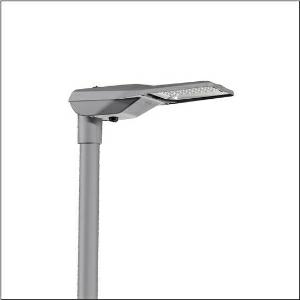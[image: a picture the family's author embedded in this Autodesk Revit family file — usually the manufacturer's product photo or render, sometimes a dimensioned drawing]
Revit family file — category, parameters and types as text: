
# Revit family: streetlight_sl_21_mini___stw1_0a_5xe2e63t08hb_eb5d
name_source: partatom
category: Lighting Fixtures
units: mm (PartAtom-declared; Revit-internal decimal feet)

## family parameters
Cut with Voids When Loaded = No
Host = Face
Light Source = No
Part Type = Normal
Room Calculation Point = No
Round Connector Dimension = Use Diameter
Shared = No

## types (1)
- --- (1 x LED, 8110 lm, 66 W, 2700K)
    Apparent Load = 66 VA
    CIE Flux Codes = 38 75 98 100 100
    Color Rendering = 70
    Color Temperature = 2700K
    Default Elevation = 1800 mm
    Description = Streetlight SL 21 mini, mast luminaire, primary light control with lens, of PMMA, primary optical cover: cover, of toughened safety glass, transparent, light distribution: STW1.0a, light emission: direct distribution, primary light characteristic: asymmetric, installation type: side-entry, post-top, LED, High Power LED, rated luminous flux: 8.110lm, luminous efficacy: 123lm/W, light colour: 727, colour temperature: 2700K, control gear: D4i, control: overheat protection, constant luminous flux control, time-dependent luminous flux control, flexible luminous flux parameterisation, pre-setting: logarithmic dimming characteristic, mains connection: 220..240V, AC, 50/60Hz, start of lifetime: 66W, end of service life: 69W, reduction: 30W, luminaire housing, of diecast aluminium, powder-coated, Siteco® metallic grey (DB 702S), corrosivity category C5 mid according to DIN EN ISO 12944, please order mast flange separately, inclination adjustable: 0°, 5°, 10°, 15°, sealing non-destructively replaceable, multi-level sealing system, length: 628mm, width: 235mm, height: 110mm, mast flange for spigot size: 42mm (side-entry): 5XC10008XM4, 60/48mm (side-entry/post-top): 5XC10108XM2, 76/60mm (side-entry/post-top): 5XC10108XM1, mounting height: 4..8m, Smart Interface below and above, protection rating (complete): IP66, insulation class (complete): insulation class II (safety insulation), certification: CE, ENEC, ENEC+, VDE, impact resistance: IK10, permissible operating ambient temperature for outdoor applications: -40..+50°C, standard-compliant lighting for roads and squares, packaging unit: 1 piece

Light Distribution: STW1.0a
    Height = 110 mm
    Lamp = 1 x LED
    Lamp Light Flux = 8110 lm
    Lamp Power = 66 W
    Lamp count = 1
    Length = 625 mm
    Luminous efficacy = 123 lm/W
    Manufacturer = Siteco
    ModVariant = No
    Model = 5XE2E63T08HB
    Number of Poles = 1
    OnlyDefault = Yes
    Power Factor = 1
    Product Name = Streetlight SL 21 mini | STW1.0a
    Product group = mast luminaire | pylon top
    ProductGroupID = 6100
    Protection Class = Protection class II
    Protection Degree = IP 66
    RLX_Detail_Level = 1
    RLX_Emergency_Light_Flux = 0 lm
    RLX_Emergency_Type = 0
    RLX_Emergency_Type_DB = No
    RlxData = <blob elided: 26241 chars, md5=2399ad0b>
    Socket = socket
    Standby Power = 0 W
    System Light Flux = 8110 lm
    System Power = 66 W
    Type Comments = factory setting: luminous flux: 100 % | dim-lin: 254 | 670 mA
    Type Image = l_1003514.jpg
    URL = http://relux.com
    VarID = @adj_187114
    Voltage = 0 V
    Weight = 0.00 kg
    Width = 234 mm

## geometry (parser evidence)
native form markers: Blend x4, Sweep x12
no freeform markers — native parametric forms only
